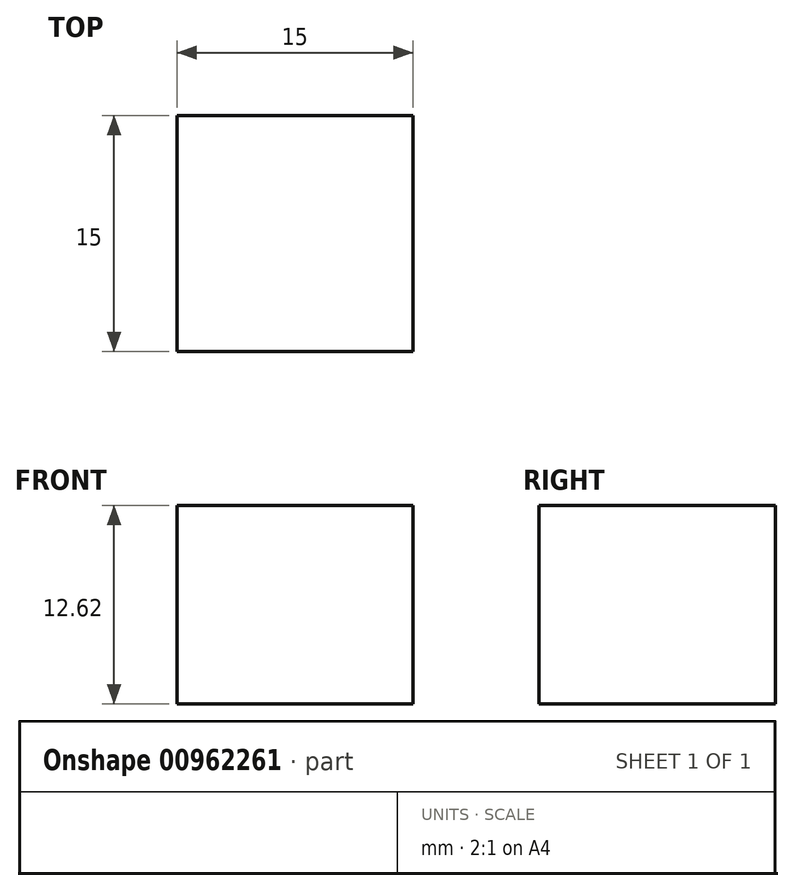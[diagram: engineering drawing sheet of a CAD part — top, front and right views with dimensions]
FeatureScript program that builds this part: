
annotation { "Feature Type Name" : "Feature", "Feature Type Description" : "" }
export const myFeature = defineFeature(function(context is Context, id is Id, definition is map)
    precondition{}
    {
        {
            var Q0;
            Q0=qCreatedBy(makeId("Front.planeOp"),FACE);
            var sketch = newSketch(context, id + "F0", { "sketchPlane" : qUnion([Q0])});
            skLineSegment(sketch, "E0.bottom", {"start": v(0, 0) * mm, "end": v(-15, 0) * mm});
            skLineSegment(sketch, "E0.top", {"start": v(0, -12.62) * mm, "end": v(-15, -12.62) * mm});
            skLineSegment(sketch, "E0.left", {"start": v(0, 0) * mm, "end": v(0, -12.62) * mm});
            skLineSegment(sketch, "E0.right", {"start": v(-15, 0) * mm, "end": v(-15, -12.62) * mm});
            skSolve(sketch);
        }
        {
            var Q0;
            Q0=makeQuery(id+"F0.imprint","IMPRINT",FACE,{"disambiguationData":[TD([[makeQuery(id+"F0.imprint","IMPRINT",EDGE,{"derivedFrom":sQuery(id+"F0.wireOp",EDGE,"E0.bottom")}),1.0]])]});
            extrude(context, id + "F1", {"entities" : qUnion([Q0]), "depth" : 15 * mm, "offsetDistance" : 25.4 * mm});
        }
    });
